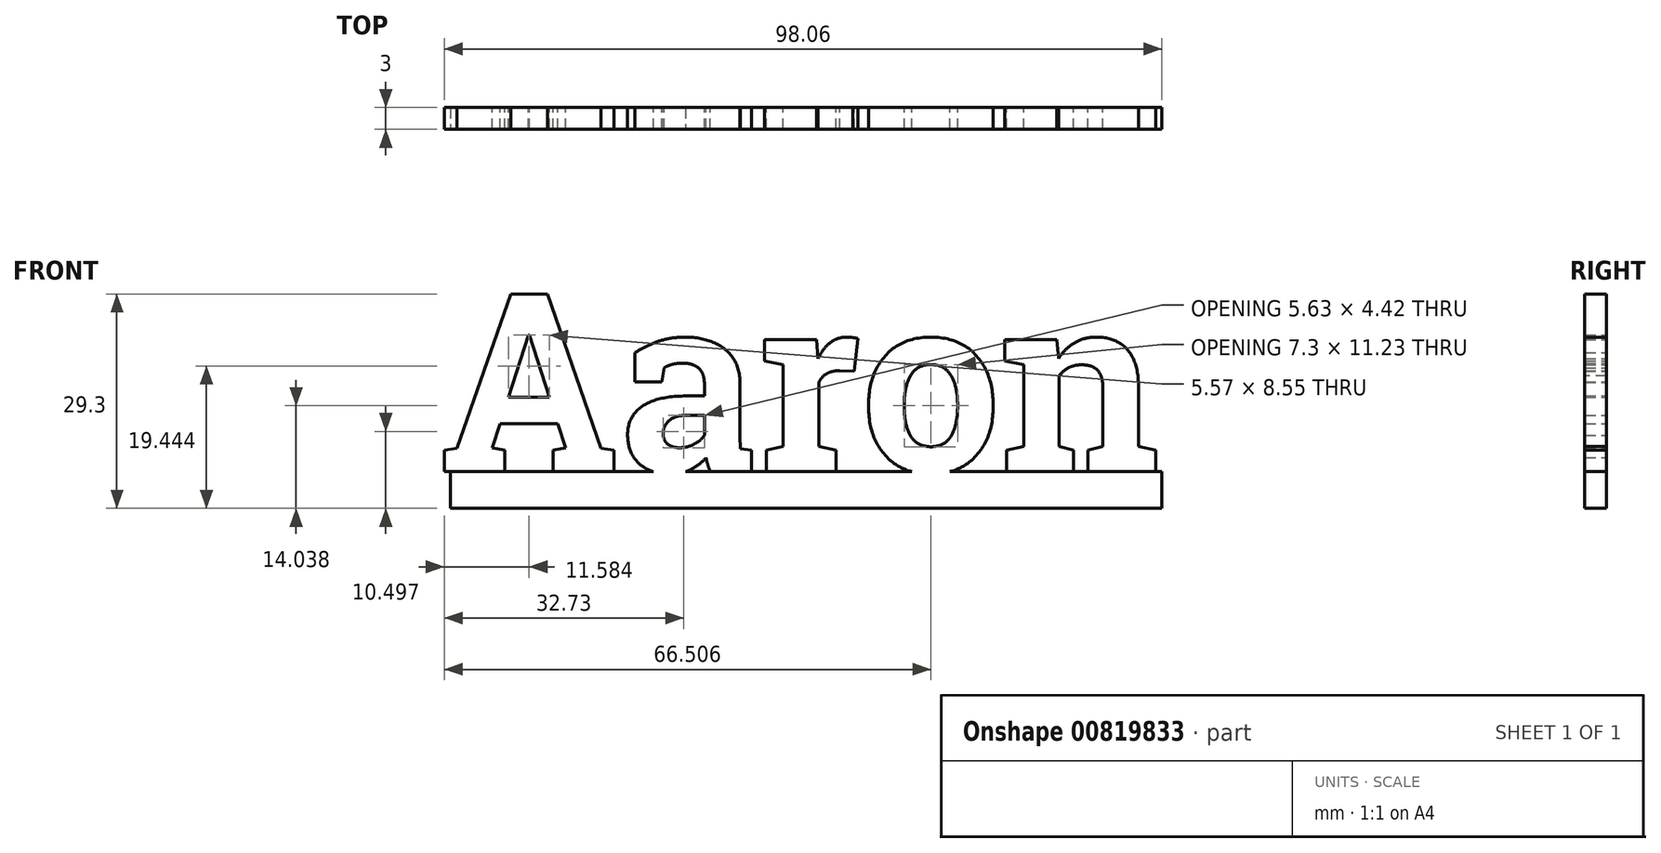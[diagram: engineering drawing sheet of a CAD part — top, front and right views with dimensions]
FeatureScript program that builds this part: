
annotation { "Feature Type Name" : "Feature", "Feature Type Description" : "" }
export const myFeature = defineFeature(function(context is Context, id is Id, definition is map)
    precondition{}
    {
        {
            var Q0;
            Q0=qCreatedBy(makeId("Front.planeOp"),FACE);
            var sketch = newSketch(context, id + "F0", { "sketchPlane" : qUnion([Q0])});
            skText(sketch, "E0", { "text": "Aaron", "fontName": "RobotoSlab-Bold.ttf"});
            const initialGuessF0  = {"E0": [-0.05082, 0.00063, 1, 0, 0.02457]};
            skSetInitialGuess(sketch, initialGuessF0);
            skSolve(sketch);
        }
        {
            var Q0;
            Q0 = qSketchRegion(id + "F0", true);
            extrude(context, id + "F1", {"entities" : qUnion([Q0]), "endBound" : BoundingType.SYMMETRIC, "depth" : 3 * mm, "offsetDistance" : 25 * mm});
        }
        {
            var Q0;
            Q0=makeQuery(id+"F1.opExtrude","CAP_FACE",FACE,{"disambiguationData":[OSD([sQuery(id+"F0.wireOp",EDGE,"E0.sketch_text.stroke-0"),sQuery(id+"F0.wireOp",EDGE,"E0.sketch_text.stroke-1"),sQuery(id+"F0.wireOp",EDGE,"E0.sketch_text.stroke-2"),sQuery(id+"F0.wireOp",EDGE,"E0.sketch_text.stroke-3"),sQuery(id+"F0.wireOp",EDGE,"E0.sketch_text.stroke-4"),sQuery(id+"F0.wireOp",EDGE,"E0.sketch_text.stroke-5"),sQuery(id+"F0.wireOp",EDGE,"E0.sketch_text.stroke-6"),sQuery(id+"F0.wireOp",EDGE,"E0.sketch_text.stroke-7"),sQuery(id+"F0.wireOp",EDGE,"E0.sketch_text.stroke-8"),sQuery(id+"F0.wireOp",EDGE,"E0.sketch_text.stroke-9"),sQuery(id+"F0.wireOp",EDGE,"E0.sketch_text.stroke-10"),sQuery(id+"F0.wireOp",EDGE,"E0.sketch_text.stroke-11"),sQuery(id+"F0.wireOp",EDGE,"E0.sketch_text.stroke-12"),sQuery(id+"F0.wireOp",EDGE,"E0.sketch_text.stroke-13"),sQuery(id+"F0.wireOp",EDGE,"E0.sketch_text.stroke-14"),sQuery(id+"F0.wireOp",EDGE,"E0.sketch_text.stroke-15"),sQuery(id+"F0.wireOp",EDGE,"E0.sketch_text.stroke-16"),sQuery(id+"F0.wireOp",EDGE,"E0.sketch_text.stroke-17"),sQuery(id+"F0.wireOp",EDGE,"E0.sketch_text.stroke-18"),sQuery(id+"F0.wireOp",EDGE,"E0.sketch_text.stroke-19")])],"isStart":false});
            var sketch = newSketch(context, id + "F2", { "sketchPlane" : qUnion([Q0])});
            skLineSegment(sketch, "E1.bottom", {"start": v(-49.32, 0.6) * mm, "end": v(47.92, 0.6) * mm});
            skLineSegment(sketch, "E1.top", {"start": v(-49.32, -4.41) * mm, "end": v(47.92, -4.41) * mm});
            skLineSegment(sketch, "E1.left", {"start": v(-49.32, 0.6) * mm, "end": v(-49.32, -4.41) * mm});
            skLineSegment(sketch, "E1.right", {"start": v(47.92, 0.6) * mm, "end": v(47.92, -4.41) * mm});
            skSolve(sketch);
        }
        {
            var Q0;
            {var subQ2=sQuery(id+"F2.wireOp",EDGE,"E1.top");Q0=makeQuery(id+"F2.imprint","IMPRINT",FACE,{"disambiguationData":[TD([[makeQuery(id+"F2.imprint","IMPRINT",EDGE,{"derivedFrom":subQ2}),1.0]])]});}
            extrude(context, id + "F3", {"entities" : qUnion([Q0]), "operationType" : NewBodyOperationType.ADD, "oppositeDirection" : true, "depth" : 3 * mm, "offsetDistance" : 25 * mm});
        }
    });
